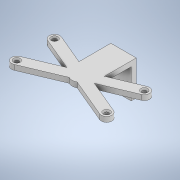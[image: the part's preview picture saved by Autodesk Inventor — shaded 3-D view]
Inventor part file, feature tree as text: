
AUTODESK INVENTOR PART (.ipt)
format: ipt  version: 2021 (Build 250183000, 183)  size: 211,968 bytes
history: native  units: mm
features: extrude x4, sketch x2, other x1, plane x1, chamfer x1
ambient origin geometry x8: Origin, YZ Plane, XZ Plane, XY Plane, X Axis, Y Axis, Z Axis, Center Point
bodies: Body1 (feature_tree)
feature tree (9):
  other  "HC-SR04.ipt"
  extrude  "Extrusion1"  Depth=10.0mm
  extrude  "Extrusion2"  Depth=5.0mm
  plane  "Arbeitsebene1"
  extrude  "Extrusion3"  Depth=5.0mm
  extrude  "Extrusion4"  Depth=5.0mm
  chamfer  "Fase1"  Distance=5.0mm
  sketch  "Skizze3"  dims[d0=10.0mm d1=2.0mm]
  sketch  "Skizze4"  dims[d3=8.0mm d5=5.0mm d6=5.0mm d7=5.0mm d8=5.0mm d9=5.0mm d10=5.0mm d11=5.0mm d12=5.0mm d13=3.0mm d14=12.0mm d15=10.0mm d16=2.4mm d17=2.4mm d18=0.0mm d19=14.0mm d20=0.0mm d21=2.4mm d22=0.0mm d23=0.0mm d25=18.439089mm d26=2.19513mm d27=5.446363mm d28=4.2mm d30=5.446363mm d31=12.0mm d32=0.0mm d33=0.6mm d34=2.0mm d35=45.0deg]
